# Revit family: BC_RHME-(120-140)AH2_LOD400_
name_source: partatom
category: Equipement de génie climatique
revit_build: Autodesk Revit 2017 (Build: 20160225_1515(x64)
units: mm (PartAtom-declared; Revit-internal decimal feet)

## family parameters
Basée sur le plan de construction = Non
Cote de connecteur circulaire = Utiliser le diamètre
Couper avec des vides une fois chargée = Non
Numéro OmniClass = 23.75.10.24
Partagée = Non
Point de calcul de pièce = Non
Titre OmniClass = Cooling and Freeze Plant
Toujours verticalement = Oui
Type d'élément = Normal

## types (2) — shared parameters
Coefficient Of Performance (COP) = 2.82
Color = Natural Grey
Description = Samurai - Air Cooled Heat Pump
Energy Efficiency Ratio (EER) = 2.93
Fabricant = HITACHI
Heating Nominal Current = 162 A
Heating Nominal Flow = 49.9 m³/h
Heating Nominal Input Power = 102 kW
Heating Power = 103 kW
Heating Pressure Drop at nominal flow = 10.7 kPa
Inlet Water Diameter = 673 mm
Maximum AC Voltage = 440 V
Maximum Air Flow = 100.8 m³/h
Minimum AC Voltage = 360 V
Modèle = Samurai - Air Cooled Heat Pump
Nominal Voltage = 400 V
Operating Mode Heat Pump = Heat Pump (5)
Overall Height = 2450 mm
Overall Length = 2300 mm
Overall Width = 3970 mm
Rated Frequency = 50 Hz
Refrigerant Type = R134a
Season Coefficient Of Performance (SCOP) = 3.22
Static Pressure = 0.0 kPa
Water Outlet Diameter = 673 mm

## per-type parameters (varying)
- Samurai - Air Cooled Heat Pump - RHME 120AH2: AXI_PDS_FCT=2820.00 kg; Cooling Airflow High=73.7 m³/h; Cooling Capacity=300 kW; Cooling Capacity Min=32 kW; Cooling Nominal Current=176 A; Cooling Nominal Flow=51.6 m³/h; Cooling Nominal Input Power=102 kW; Cooling Power=102 kW; Cooling Pressure Drop at nominal flow=11.4 kPa; Extra Super Low Noise Model (dB(A))=91; Extra Super Low Noise Model at 10m (dB(A))=63; Heating Airflow High=73.7 m³/h; Heating Capacity=290 kW; Heating Capacity Min=32 kW; Heating Sound Level Low (dB)=96; Heating Sound Level Silent (dB)=99; Low Noise Model at 10m (dB(A))=68; Maximum Current for cable sizing=238 A; Maximum Input Power for cable sizing=138 kW; Maximum Starting Current for cable sizing=259 A; Product Code=9E121342; Refrigerant Quantity=74.00 kg; Seasonal Energy Efficiency Ratio (SEER)=3.94; Standard Noise Level Model at 10m (dB(A))=71; Starting Current=259 A; Super Low Noise Model (dB(A))=94; Super Low Noise Model at 10m (dB(A))=66; Weight Packing=2800.00 kg
- Samurai - Air Cooled Heat Pump - RHME 140AH2: AXI_PDS_FCT=2880.00 kg; Cooling Airflow High=83.5 m³/h; Cooling Capacity=339 kW; Cooling Capacity Min=37 kW; Cooling Nominal Current=199 A; Cooling Nominal Flow=58.5 m³/h; Cooling Nominal Input Power=116 kW; Cooling Power=116 kW; Cooling Pressure Drop at nominal flow=14.3 kPa; Extra Super Low Noise Model (dB(A))=92; Extra Super Low Noise Model at 10m (dB(A))=64; Heating Airflow High=83.5 m³/h; Heating Capacity=291 kW; Heating Capacity Min=37 kW; Heating Sound Level Low (dB)=97; Heating Sound Level Silent (dB)=100; Low Noise Model at 10m (dB(A))=69; Maximum Current for cable sizing=266 A; Maximum Input Power for cable sizing=155 kW; Maximum Starting Current for cable sizing=262 A; Product Code=9E141342; Refrigerant Quantity=78.00 kg; Seasonal Energy Efficiency Ratio (SEER)=3.93; Standard Noise Level Model at 10m (dB(A))=72; Starting Current=262 A; Super Low Noise Model (dB(A))=95; Super Low Noise Model at 10m (dB(A))=67; Weight Packing=2860.00 kg

note: column(s) folded — value = type name in every type: Commentaires du type
